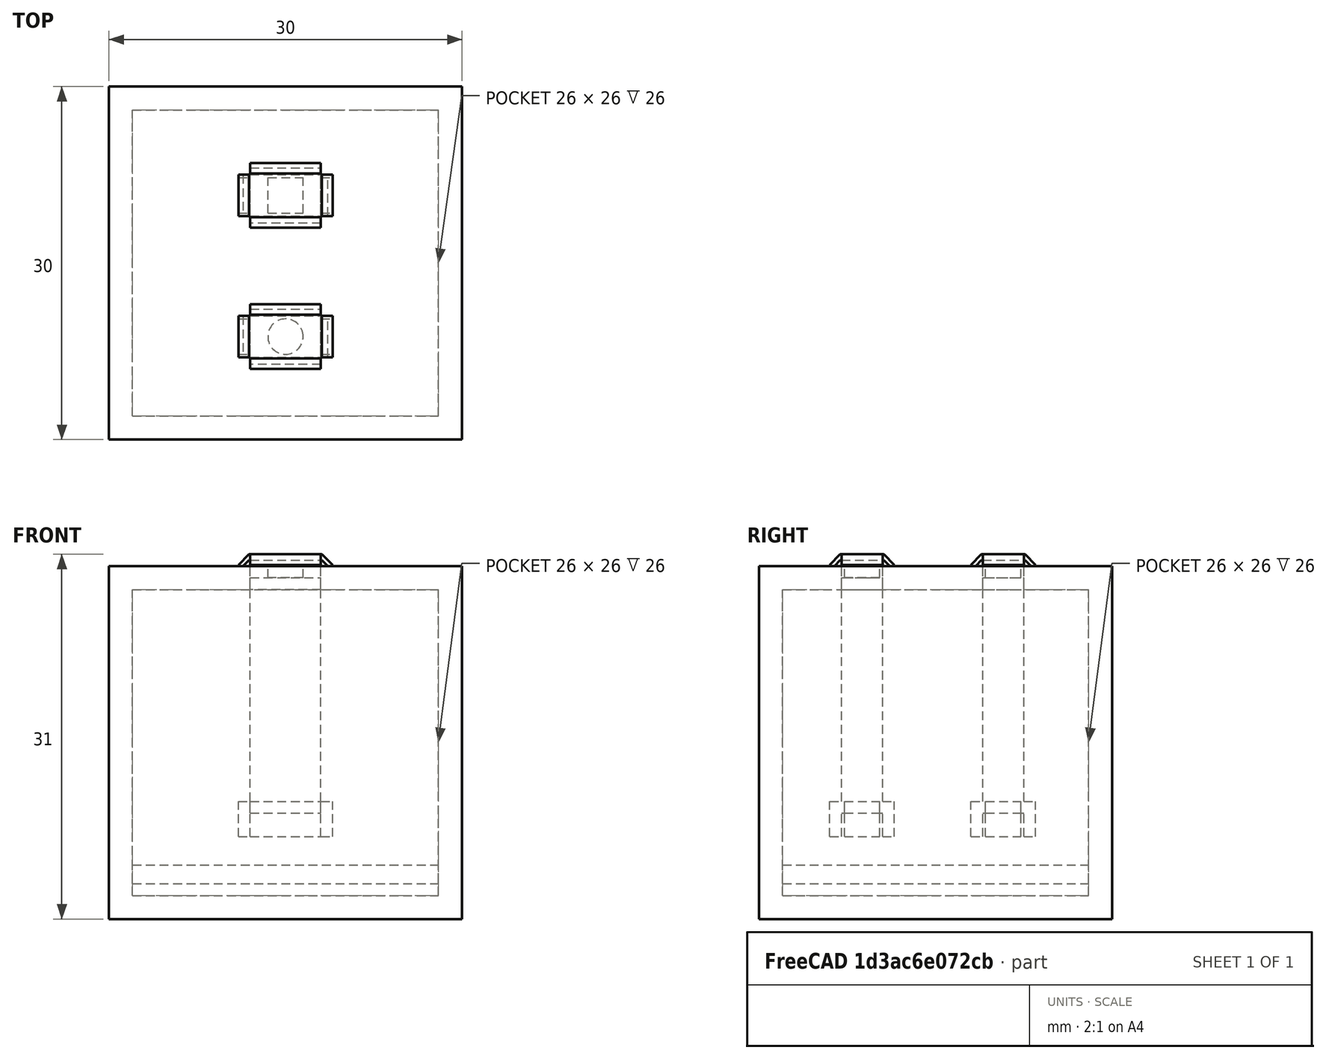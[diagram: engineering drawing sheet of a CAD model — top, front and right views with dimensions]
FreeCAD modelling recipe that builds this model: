
FCSTD DOCUMENT  (FreeCAD 0.15R4671 (Git))
Label: Button_V01
License: All rights reserved
LicenseURL: http://en.wikipedia.org/wiki/All_rights_reserved
objects: Part::Box×36, Part::MultiFuse×10, Part::Cut×4, Part::Chamfer×4, Mesh::Feature×2, Part::Cylinder×1
note: 55 computed .brp shape members not serialized (recipe doc carries the construction recipe); baked Part::Feature solids carry a one-line shape summary decoded from their .brp

FEATURE [Part::Box] Box  label="Box_out"
  Height = 30
  Length = 30
  Width = 30
FEATURE [Part::Box] Box001  label="Box_in"
  Height = 26
  Length = 26
  Placement = pos=(2,2,2) rot=(0,0,1;0rad)
  Width = 26
FEATURE [Part::Cut] Cut  label="BoX"
  Base = -> Box
  Tool = -> Box001
FEATURE [Mesh::Feature] Button_TC_1101T_C_A_B  label="Button_TC-1101T-C-A-B"
  Placement = pos=(12,7,4.6) rot=(0,0,1;0rad)
FEATURE [Part::Box] Box002  label="PCB"
  Height = 1.6
  Length = 26
  Placement = pos=(2,2,3) rot=(0,0,1;0rad)
  Width = 26
FEATURE [Mesh::Feature] Button_TC_1101T_C_A_B001  label="Button_TC-1101T-C-A-B001"
  Placement = pos=(12,19,4.6) rot=(0,0,1;0rad)
FEATURE [Part::Box] Box003  label="Button1_001"
  Height = 20
  Length = 6
  Placement = pos=(12,7,9) rot=(0,0,1;0rad)
  Width = 3.5
FEATURE [Part::Box] Box004  label="Button1_002"
  Height = 3
  Length = 1
  Placement = pos=(11,7.25,7) rot=(0,0,1;0rad)
  Width = 3
FEATURE [Part::Box] Box005  label="Button1_003"
  Height = 3
  Length = 1
  Placement = pos=(18,7.25,7) rot=(0,0,1;0rad)
  Width = 3
FEATURE [Part::Box] Box006  label="Button1_004"
  Height = 3
  Length = 6
  Placement = pos=(12,6,7) rot=(0,0,1;0rad)
  Width = 1
FEATURE [Part::Box] Box007  label="Button1_005"
  Height = 3
  Length = 6
  Placement = pos=(12,10.5,7) rot=(0,0,1;0rad)
  Width = 1
FEATURE [Part::Cylinder] Cylinder  label="Button1_006"
  Angle = 360
  Height = 10
  Placement = pos=(15,8.75,20) rot=(0,0,1;0rad)
  Radius = 1.5
FEATURE [Part::MultiFuse] Fusion  label="Button_Extender001"
  Shapes = -> [Box003,Box004,Box005,Box006,Box007]
FEATURE [Part::Box] Box008  label="Button2_007"
  Height = 20
  Length = 6
  Placement = pos=(12,7,9) rot=(0,0,1;0rad)
  Width = 3.5
FEATURE [Part::Box] Box009  label="Button2_008"
  Height = 3
  Length = 1
  Placement = pos=(11,7.25,7) rot=(0,0,1;0rad)
  Width = 3
FEATURE [Part::Box] Box010  label="Button2_009"
  Height = 3
  Length = 1
  Placement = pos=(18,7.25,7) rot=(0,0,1;0rad)
  Width = 3
FEATURE [Part::Box] Box011  label="Button2_010"
  Height = 3
  Length = 6
  Placement = pos=(12,6,7) rot=(0,0,1;0rad)
  Width = 1
FEATURE [Part::Box] Box012  label="Button2_011"
  Height = 3
  Length = 6
  Placement = pos=(12,10.5,7) rot=(0,0,1;0rad)
  Width = 1
FEATURE [Part::MultiFuse] Fusion001  label="Button_Extender002"
  Placement = pos=(0,12,0) rot=(0,0,1;0rad)
  Shapes = -> [Box008,Box009,Box010,Box011,Box012]
FEATURE [Part::Box] Box013  label="Button2_006"
  Height = 10
  Length = 3
  Placement = pos=(13.5,19.25,20) rot=(0,0,1;0rad)
  Width = 3
FEATURE [Part::Box] Box014  label="Button1_box0001"
  Height = 3
  Length = 6
  Placement = pos=(12,7,27) rot=(0,0,1;0rad)
  Width = 3.5
FEATURE [Part::Box] Box015  label="Button2_box0001"
  Height = 3
  Length = 6
  Placement = pos=(12,19,27) rot=(0,0,1;0rad)
  Width = 3.5
FEATURE [Part::Box] Box016  label="Button1_box0002"
  Height = 2
  Length = 6
  Placement = pos=(12,7,28) rot=(0,0,1;0rad)
  Width = 3.5
FEATURE [Part::Box] Box017  label="Button2_box0002"
  Height = 2
  Length = 6
  Placement = pos=(12,19,28) rot=(0,0,1;0rad)
  Width = 3.5
FEATURE [Part::Box] Box018  label="Button1_box0003"
  Height = 2
  Length = 1
  Placement = pos=(11,7,28) rot=(0,0,1;0rad)
  Width = 3.5
FEATURE [Part::Box] Box019  label="Button1_box0004"
  Height = 2
  Length = 1
  Placement = pos=(18,7,28) rot=(0,0,1;0rad)
  Width = 3.5
FEATURE [Part::Box] Box020  label="Button1_box0005"
  Height = 2
  Length = 6
  Placement = pos=(12,6,28) rot=(0,0,1;0rad)
  Width = 1
FEATURE [Part::Box] Box021  label="Button1_box0006"
  Height = 2
  Length = 6
  Placement = pos=(12,10.5,28) rot=(0,0,1;0rad)
  Width = 1
FEATURE [Part::MultiFuse] Fusion002
  Placement = pos=(0,0,1) rot=(0,0,1;0rad)
  Shapes = -> [Box021,Box020,Box019,Box018,Box016]
FEATURE [Part::Box] Box022  label="Button2_box0003"
  Height = 2
  Length = 1
  Placement = pos=(11,19,28) rot=(0,0,1;0rad)
  Width = 3.5
FEATURE [Part::Box] Box023  label="Button2_box0004"
  Height = 2
  Length = 1
  Placement = pos=(18,19,28) rot=(0,0,1;0rad)
  Width = 3.5
FEATURE [Part::Box] Box024  label="Button2_box0005"
  Height = 2
  Length = 6
  Placement = pos=(12,18,28) rot=(0,0,1;0rad)
  Width = 1
FEATURE [Part::Box] Box025  label="Button2_box0006"
  Height = 2
  Length = 6
  Placement = pos=(12,22.5,28) rot=(0,0,1;0rad)
  Width = 1
FEATURE [Part::MultiFuse] Fusion003
  Placement = pos=(0,0,1) rot=(0,0,1;0rad)
  Shapes = -> [Box025,Box024,Box023,Box022,Box017]
FEATURE [Part::MultiFuse] Fusion004  label="Fusion004_cut"
  Shapes = -> [Box015,Box014]
FEATURE [Part::Cut] Cut001
  Base = -> Cut
  Tool = -> Fusion004
FEATURE [Part::Chamfer] Chamfer  label="ChamferBt1"
  Base = -> Fusion002
  Edges = 4 edges r=0.9: [Edge2,Edge27,Edge30,Edge34]
FEATURE [Part::Chamfer] Chamfer001  label="Chamfer001Bt2"
  Base = -> Fusion003
  Edges = 4 edges r=0.9: [Edge2,Edge27,Edge30,Edge34]
FEATURE [Part::MultiFuse] Fusion005  label="Bt_Ex1"
  Shapes = -> [Fusion,Cylinder]
FEATURE [Part::MultiFuse] Fusion006  label="Bt_Ex2"
  Shapes = -> [Fusion001,Box013]
FEATURE [Part::Box] Box026  label="Button1_box0007"
  Height = 2
  Length = 6
  Placement = pos=(12,7,28) rot=(0,0,1;0rad)
  Width = 3.5
FEATURE [Part::Box] Box027  label="Button1_box0008"
  Height = 2
  Length = 1
  Placement = pos=(11,7,28) rot=(0,0,1;0rad)
  Width = 3.5
FEATURE [Part::Box] Box028  label="Button1_box0009"
  Height = 2
  Length = 1
  Placement = pos=(18,7,28) rot=(0,0,1;0rad)
  Width = 3.5
FEATURE [Part::Box] Box029  label="Button1_box0010"
  Height = 2
  Length = 6
  Placement = pos=(12,6,28) rot=(0,0,1;0rad)
  Width = 1
FEATURE [Part::Box] Box030  label="Button1_box0011"
  Height = 2
  Length = 6
  Placement = pos=(12,10.5,28) rot=(0,0,1;0rad)
  Width = 1
FEATURE [Part::MultiFuse] Fusion007
  Placement = pos=(0,0,1) rot=(0,0,1;0rad)
  Shapes = -> [Box030,Box029,Box028,Box027,Box026]
FEATURE [Part::Chamfer] Chamfer002  label="Chamfer002Bt1"
  Base = -> Fusion007
  Edges = 4 edges r=0.9: [Edge2,Edge27,Edge30,Edge34]
  Placement = pos=(0,0,-0.5) rot=(0,0,1;0rad)
FEATURE [Part::Box] Box031  label="Button2_box0007"
  Height = 2
  Length = 6
  Placement = pos=(12,19,28) rot=(0,0,1;0rad)
  Width = 3.5
FEATURE [Part::Box] Box032  label="Button2_box0008"
  Height = 2
  Length = 1
  Placement = pos=(11,19,28) rot=(0,0,1;0rad)
  Width = 3.5
FEATURE [Part::Box] Box033  label="Button2_box0009"
  Height = 2
  Length = 1
  Placement = pos=(18,19,28) rot=(0,0,1;0rad)
  Width = 3.5
FEATURE [Part::Box] Box034  label="Button2_box0010"
  Height = 2
  Length = 6
  Placement = pos=(12,18,28) rot=(0,0,1;0rad)
  Width = 1
FEATURE [Part::Box] Box035  label="Button2_box0011"
  Height = 2
  Length = 6
  Placement = pos=(12,22.5,28) rot=(0,0,1;0rad)
  Width = 1
FEATURE [Part::MultiFuse] Fusion008
  Placement = pos=(0,0,1) rot=(0,0,1;0rad)
  Shapes = -> [Box035,Box034,Box033,Box032,Box031]
FEATURE [Part::Chamfer] Chamfer003  label="Chamfer002Bt2"
  Base = -> Fusion008
  Edges = 4 edges r=0.9: [Edge2,Edge27,Edge30,Edge34]
  Placement = pos=(0,0,-0.5) rot=(0,0,1;0rad)
FEATURE [Part::Cut] Cut002
  Base = -> Chamfer
  Tool = -> Chamfer002
FEATURE [Part::Cut] Cut003
  Base = -> Chamfer001
  Tool = -> Chamfer003
FEATURE [Part::MultiFuse] Fusion009  label="BOX"
  Shapes = -> [Cut002,Cut003,Cut001]
